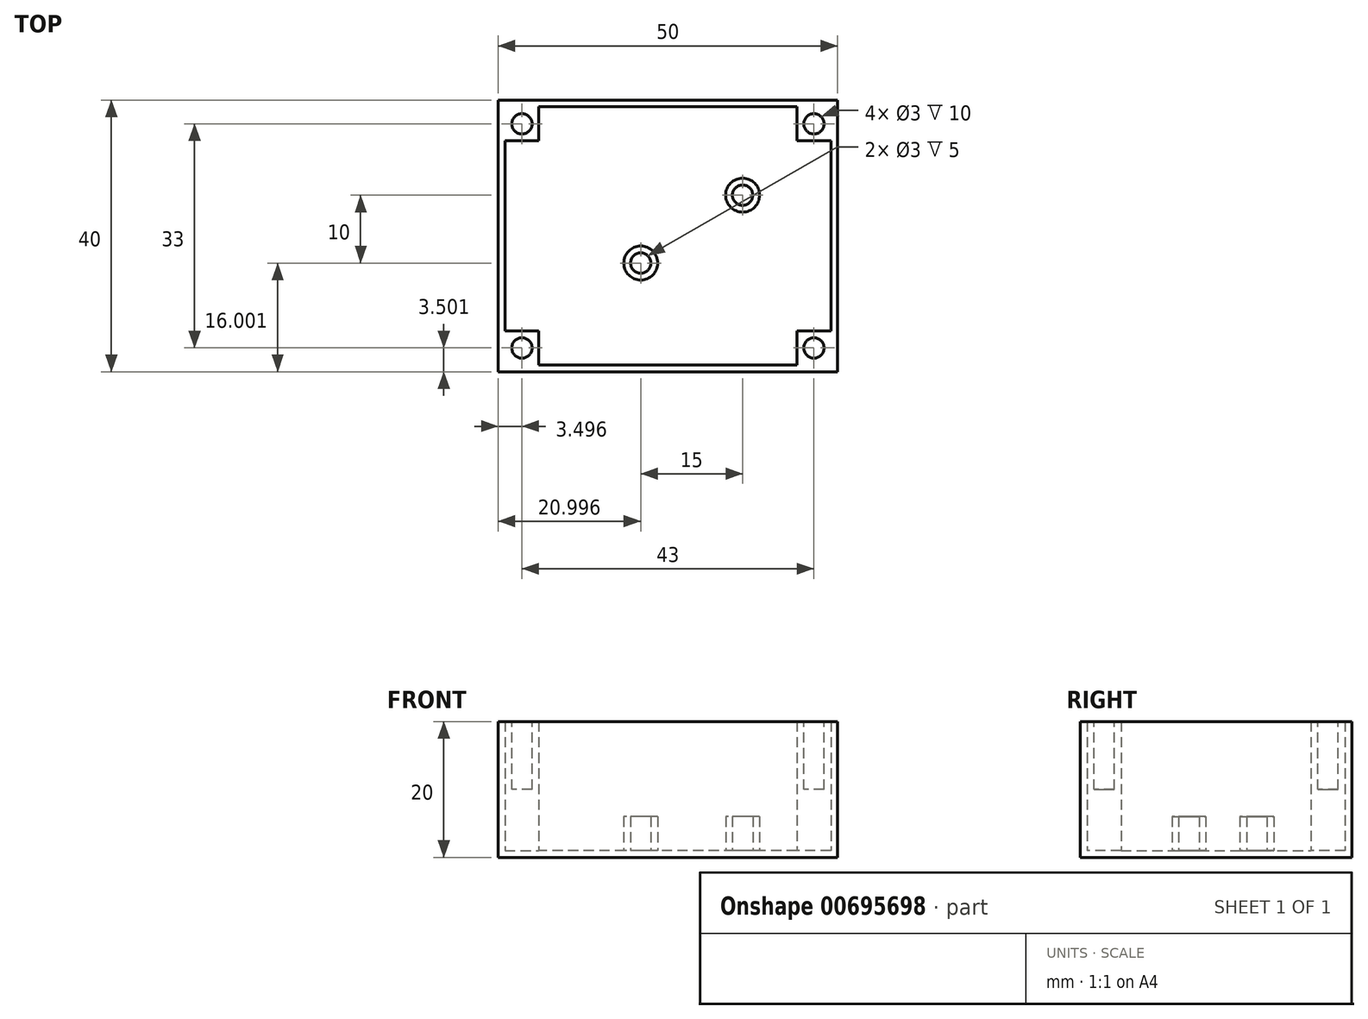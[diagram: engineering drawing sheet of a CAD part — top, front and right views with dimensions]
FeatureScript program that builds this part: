
annotation { "Feature Type Name" : "Feature", "Feature Type Description" : "" }
export const myFeature = defineFeature(function(context is Context, id is Id, definition is map)
    precondition{}
    {
        {
            var Q0;
            Q0=qCreatedBy(makeId("Top.planeOp"),FACE);
            var sketch = newSketch(context, id + "F0", { "sketchPlane" : qUnion([Q0])});
            skLineSegment(sketch, "E0.bottom", {"start": v(-64.05, 56.97) * mm, "end": v(-14.05, 56.97) * mm});
            skLineSegment(sketch, "E0.top", {"start": v(-64.05, 16.97) * mm, "end": v(-14.05, 16.97) * mm});
            skLineSegment(sketch, "E0.left", {"start": v(-64.05, 56.97) * mm, "end": v(-64.05, 16.97) * mm});
            skLineSegment(sketch, "E0.right", {"start": v(-14.05, 56.97) * mm, "end": v(-14.05, 16.97) * mm});
            skSolve(sketch);
        }
        {
            var Q0;
            Q0=makeQuery(id+"F0.imprint","IMPRINT",FACE,{"disambiguationData":[TD([[makeQuery(id+"F0.imprint","IMPRINT",EDGE,{"derivedFrom":sQuery(id+"F0.wireOp",EDGE,"E0.bottom")}),-1.0]])]});
            extrude(context, id + "F1", {"entities" : qUnion([Q0]), "depth" : 20 * mm, "offsetDistance" : 25 * mm});
        }
        {
            var Q0;
            Q0=makeQuery(id+"F1.opExtrude","CAP_FACE",FACE,{"disambiguationData":[OSD([sQuery(id+"F0.wireOp",EDGE,"E0.bottom"),sQuery(id+"F0.wireOp",EDGE,"E0.top"),sQuery(id+"F0.wireOp",EDGE,"E0.left"),sQuery(id+"F0.wireOp",EDGE,"E0.right")])],"isStart":false});
            var sketch = newSketch(context, id + "F2", { "sketchPlane" : qUnion([Q0])});
            skLineSegment(sketch, "E1.bottom", {"start": v(-15.05, 17.97) * mm, "end": v(-63.05, 17.97) * mm});
            skLineSegment(sketch, "E1.top", {"start": v(-15.05, 55.97) * mm, "end": v(-63.05, 55.97) * mm});
            skLineSegment(sketch, "E1.left", {"start": v(-15.05, 17.97) * mm, "end": v(-15.05, 55.97) * mm});
            skLineSegment(sketch, "E1.right", {"start": v(-63.05, 17.97) * mm, "end": v(-63.05, 55.97) * mm});
            skPoint(sketch, "E1.middle", {"position": v(-39.05, 36.97) * mm});
            skPoint(sketch, "E1.middle.positionSnap0", {"position": v(-64.05, 36.97) * mm});
            skPoint(sketch, "E1.middle.positionSnap1", {"position": v(-39.05, 16.97) * mm});
            skPoint(sketch, "E1.centerSnap0", {"position": v(-64.05, 36.97) * mm});
            skPoint(sketch, "E1.centerSnap1", {"position": v(-39.05, 16.97) * mm});
            skSolve(sketch);
        }
        {
            var Q0;
            Q0=makeQuery(id+"F2.imprint","IMPRINT",FACE,{"disambiguationData":[TD([[makeQuery(id+"F2.imprint","IMPRINT",EDGE,{"derivedFrom":sQuery(id+"F2.wireOp",EDGE,"E1.bottom")}),-1.0]])]});
            extrude(context, id + "F3", {"entities" : qUnion([Q0]), "operationType" : NewBodyOperationType.REMOVE, "oppositeDirection" : true, "depth" : 19 * mm, "offsetDistance" : 25 * mm});
        }
        {
            var Q0;
            Q0=makeQuery(id+"F3.boolean.opBoolean","COPY",FACE,{"derivedFrom":makeQuery(id+"F3.opExtrude","CAP_FACE",FACE,{"disambiguationData":[OSD([sQuery(id+"F2.wireOp",EDGE,"E1.bottom"),sQuery(id+"F2.wireOp",EDGE,"E1.top"),sQuery(id+"F2.wireOp",EDGE,"E1.left"),sQuery(id+"F2.wireOp",EDGE,"E1.right")])],"isStart":false})});
            var sketch = newSketch(context, id + "F4", { "sketchPlane" : qUnion([Q0])});
            skLineSegment(sketch, "E2.bottom", {"start": v(-63.05, 55.97) * mm, "end": v(-58.05, 55.97) * mm});
            skLineSegment(sketch, "E2.top", {"start": v(-63.05, 50.97) * mm, "end": v(-58.05, 50.97) * mm});
            skLineSegment(sketch, "E2.left", {"start": v(-63.05, 55.97) * mm, "end": v(-63.05, 50.97) * mm});
            skLineSegment(sketch, "E2.right", {"start": v(-58.05, 55.97) * mm, "end": v(-58.05, 50.97) * mm});
            skLineSegment(sketch, "E3.bottom", {"start": v(-15.05, 55.97) * mm, "end": v(-20.05, 55.97) * mm});
            skLineSegment(sketch, "E3.top", {"start": v(-15.05, 50.97) * mm, "end": v(-20.05, 50.97) * mm});
            skLineSegment(sketch, "E3.left", {"start": v(-15.05, 55.97) * mm, "end": v(-15.05, 50.97) * mm});
            skLineSegment(sketch, "E3.right", {"start": v(-20.05, 55.97) * mm, "end": v(-20.05, 50.97) * mm});
            skLineSegment(sketch, "E4.bottom", {"start": v(-63.05, 22.97) * mm, "end": v(-58.05, 22.97) * mm});
            skLineSegment(sketch, "E4.top", {"start": v(-63.05, 17.97) * mm, "end": v(-58.05, 17.97) * mm});
            skLineSegment(sketch, "E4.left", {"start": v(-63.05, 22.97) * mm, "end": v(-63.05, 17.97) * mm});
            skLineSegment(sketch, "E4.right", {"start": v(-58.05, 22.97) * mm, "end": v(-58.05, 17.97) * mm});
            skLineSegment(sketch, "E5.bottom", {"start": v(-15.05, 22.97) * mm, "end": v(-20.05, 22.97) * mm});
            skLineSegment(sketch, "E5.top", {"start": v(-15.05, 17.97) * mm, "end": v(-20.05, 17.97) * mm});
            skLineSegment(sketch, "E5.left", {"start": v(-15.05, 22.97) * mm, "end": v(-15.05, 17.97) * mm});
            skLineSegment(sketch, "E5.right", {"start": v(-20.05, 22.97) * mm, "end": v(-20.05, 17.97) * mm});
            skSolve(sketch);
        }
        {
            var Q0;
            Q0=makeQuery(id+"F4.imprint","IMPRINT",FACE,{"disambiguationData":[TD([[makeQuery(id+"F4.imprint","IMPRINT",EDGE,{"derivedFrom":sQuery(id+"F4.wireOp",EDGE,"E2.bottom")}),1.0]])]});
            var Q1;
            Q1=makeQuery(id+"F4.imprint","IMPRINT",FACE,{"disambiguationData":[TD([[makeQuery(id+"F4.imprint","IMPRINT",EDGE,{"derivedFrom":sQuery(id+"F4.wireOp",EDGE,"E4.bottom")}),-1.0]])]});
            var Q2;
            Q2=makeQuery(id+"F4.imprint","IMPRINT",FACE,{"disambiguationData":[TD([[makeQuery(id+"F4.imprint","IMPRINT",EDGE,{"derivedFrom":sQuery(id+"F4.wireOp",EDGE,"E3.bottom")}),1.0]])]});
            var Q3;
            Q3=makeQuery(id+"F4.imprint","IMPRINT",FACE,{"disambiguationData":[TD([[makeQuery(id+"F4.imprint","IMPRINT",EDGE,{"derivedFrom":sQuery(id+"F4.wireOp",EDGE,"E5.bottom")}),1.0]])]});
            extrude(context, id + "F5", {"entities" : qUnion([Q0, Q1, Q2, Q3]), "operationType" : NewBodyOperationType.ADD, "depth" : 19 * mm, "offsetDistance" : 25 * mm});
        }
        {
            var Q0;
            Q0=makeQuery(id+"F5.boolean.opBoolean","MERGE",FACE,{"derivedFrom":[makeQuery(id+"F1.opExtrude","CAP_FACE",FACE,{"disambiguationData":[OSD([sQuery(id+"F0.wireOp",EDGE,"E0.bottom"),sQuery(id+"F0.wireOp",EDGE,"E0.top"),sQuery(id+"F0.wireOp",EDGE,"E0.left"),sQuery(id+"F0.wireOp",EDGE,"E0.right")])],"isStart":false}),makeQuery(id+"F5.opExtrude","CAP_FACE",FACE,{"disambiguationData":[OSD([sQuery(id+"F4.wireOp",EDGE,"E2.bottom"),sQuery(id+"F4.wireOp",EDGE,"E2.top"),sQuery(id+"F4.wireOp",EDGE,"E2.left"),sQuery(id+"F4.wireOp",EDGE,"E2.right")])],"isStart":false}),makeQuery(id+"F5.opExtrude","CAP_FACE",FACE,{"disambiguationData":[OSD([sQuery(id+"F4.wireOp",EDGE,"E3.bottom"),sQuery(id+"F4.wireOp",EDGE,"E3.top"),sQuery(id+"F4.wireOp",EDGE,"E3.left"),sQuery(id+"F4.wireOp",EDGE,"E3.right")])],"isStart":false}),makeQuery(id+"F5.opExtrude","CAP_FACE",FACE,{"disambiguationData":[OSD([sQuery(id+"F4.wireOp",EDGE,"E4.bottom"),sQuery(id+"F4.wireOp",EDGE,"E4.top"),sQuery(id+"F4.wireOp",EDGE,"E4.left"),sQuery(id+"F4.wireOp",EDGE,"E4.right")])],"isStart":false}),makeQuery(id+"F5.opExtrude","CAP_FACE",FACE,{"disambiguationData":[OSD([sQuery(id+"F4.wireOp",EDGE,"E5.bottom"),sQuery(id+"F4.wireOp",EDGE,"E5.top"),sQuery(id+"F4.wireOp",EDGE,"E5.left"),sQuery(id+"F4.wireOp",EDGE,"E5.right")])],"isStart":false})]});
            var sketch = newSketch(context, id + "F6", { "sketchPlane" : qUnion([Q0])});
            skCircle(sketch, "E6", {"center": v(-60.55, 20.47) * mm, "radius": 1.5 * mm});
            skPoint(sketch, "E6.centerSnap0", {"position": v(-58.05, 20.47) * mm});
            skPoint(sketch, "E6.centerSnap1", {"position": v(-60.55, 22.97) * mm});
            skCircle(sketch, "E7", {"center": v(-60.55, 53.47) * mm, "radius": 1.5 * mm});
            skPoint(sketch, "E7.centerSnap0", {"position": v(-58.05, 53.47) * mm});
            skPoint(sketch, "E7.centerSnap1", {"position": v(-60.55, 50.97) * mm});
            skCircle(sketch, "E8", {"center": v(-17.55, 53.47) * mm, "radius": 1.5 * mm});
            skPoint(sketch, "E8.centerSnap0", {"position": v(-17.55, 50.97) * mm});
            skPoint(sketch, "E8.centerSnap1", {"position": v(-20.05, 53.47) * mm});
            skCircle(sketch, "E9", {"center": v(-17.55, 20.47) * mm, "radius": 1.5 * mm});
            skPoint(sketch, "E9.centerSnap0", {"position": v(-20.05, 20.47) * mm});
            skPoint(sketch, "E9.centerSnap1", {"position": v(-17.55, 22.97) * mm});
            skSolve(sketch);
        }
        {
            var Q0;
            Q0=makeQuery(id+"F6.imprint","IMPRINT",FACE,{"disambiguationData":[TD([[makeQuery(id+"F6.imprint","IMPRINT",EDGE,{"derivedFrom":sQuery(id+"F6.wireOp",EDGE,"E7")}),1.0]])]});
            var Q1;
            Q1=makeQuery(id+"F6.imprint","IMPRINT",FACE,{"disambiguationData":[TD([[makeQuery(id+"F6.imprint","IMPRINT",EDGE,{"derivedFrom":sQuery(id+"F6.wireOp",EDGE,"E6")}),1.0]])]});
            var Q2;
            Q2=makeQuery(id+"F6.imprint","IMPRINT",FACE,{"disambiguationData":[TD([[makeQuery(id+"F6.imprint","IMPRINT",EDGE,{"derivedFrom":sQuery(id+"F6.wireOp",EDGE,"E9")}),1.0]])]});
            var Q3;
            Q3=makeQuery(id+"F6.imprint","IMPRINT",FACE,{"disambiguationData":[TD([[makeQuery(id+"F6.imprint","IMPRINT",EDGE,{"derivedFrom":sQuery(id+"F6.wireOp",EDGE,"E8")}),1.0]])]});
            extrude(context, id + "F7", {"entities" : qUnion([Q0, Q1, Q2, Q3]), "operationType" : NewBodyOperationType.REMOVE, "oppositeDirection" : true, "depth" : 10 * mm, "offsetDistance" : 25 * mm});
        }
        {
            var Q0;
            Q0=makeQuery(id+"F3.boolean.opBoolean","COPY",FACE,{"derivedFrom":makeQuery(id+"F3.opExtrude","CAP_FACE",FACE,{"disambiguationData":[OSD([sQuery(id+"F2.wireOp",EDGE,"E1.bottom"),sQuery(id+"F2.wireOp",EDGE,"E1.top"),sQuery(id+"F2.wireOp",EDGE,"E1.left"),sQuery(id+"F2.wireOp",EDGE,"E1.right")])],"isStart":false})});
            var sketch = newSketch(context, id + "F8", { "sketchPlane" : qUnion([Q0])});
            skSolve(sketch);
        }
        {
            var Q0;
            Q0=makeQuery(id+"F8.imprint","IMPRINT",FACE,{"disambiguationData":[TD([[makeQuery(id+"F8.imprint","IMPRINT",EDGE,{"derivedFrom":makeQuery(id+"F3.boolean.opBoolean","COPY",EDGE,{"derivedFrom":makeQuery(id+"F3.opExtrude","CAP_EDGE",EDGE,{"disambiguationData":[OSD([sQuery(id+"F2.wireOp",EDGE,"E1.bottom")])],"isStart":false})})}),-1.0]])]});
            var sketch = newSketch(context, id + "F9", { "sketchPlane" : qUnion([Q0])});
            skCircle(sketch, "E10", {"center": v(-43.05, 32.97) * mm, "radius": 2.5 * mm});
            skCircle(sketch, "E11", {"center": v(-28.05, 42.97) * mm, "radius": 2.5 * mm});
            skCircle(sketch, "E12", {"center": v(-43.05, 32.97) * mm, "radius": 1.5 * mm});
            skCircle(sketch, "E13", {"center": v(-28.05, 42.97) * mm, "radius": 1.5 * mm});
            skSolve(sketch);
        }
        {
            var Q0;
            Q0=makeQuery(id+"F9.imprint","IMPRINT",FACE,{"disambiguationData":[TD([[makeQuery(id+"F9.imprint","IMPRINT",EDGE,{"derivedFrom":sQuery(id+"F9.wireOp",EDGE,"E10")}),1.0]])]});
            var Q1;
            Q1=makeQuery(id+"F9.imprint","IMPRINT",FACE,{"disambiguationData":[TD([[makeQuery(id+"F9.imprint","IMPRINT",EDGE,{"derivedFrom":sQuery(id+"F9.wireOp",EDGE,"E11")}),1.0]])]});
            extrude(context, id + "F10", {"entities" : qUnion([Q0, Q1]), "operationType" : NewBodyOperationType.ADD, "depth" : 5 * mm, "offsetDistance" : 25 * mm});
        }
    });
